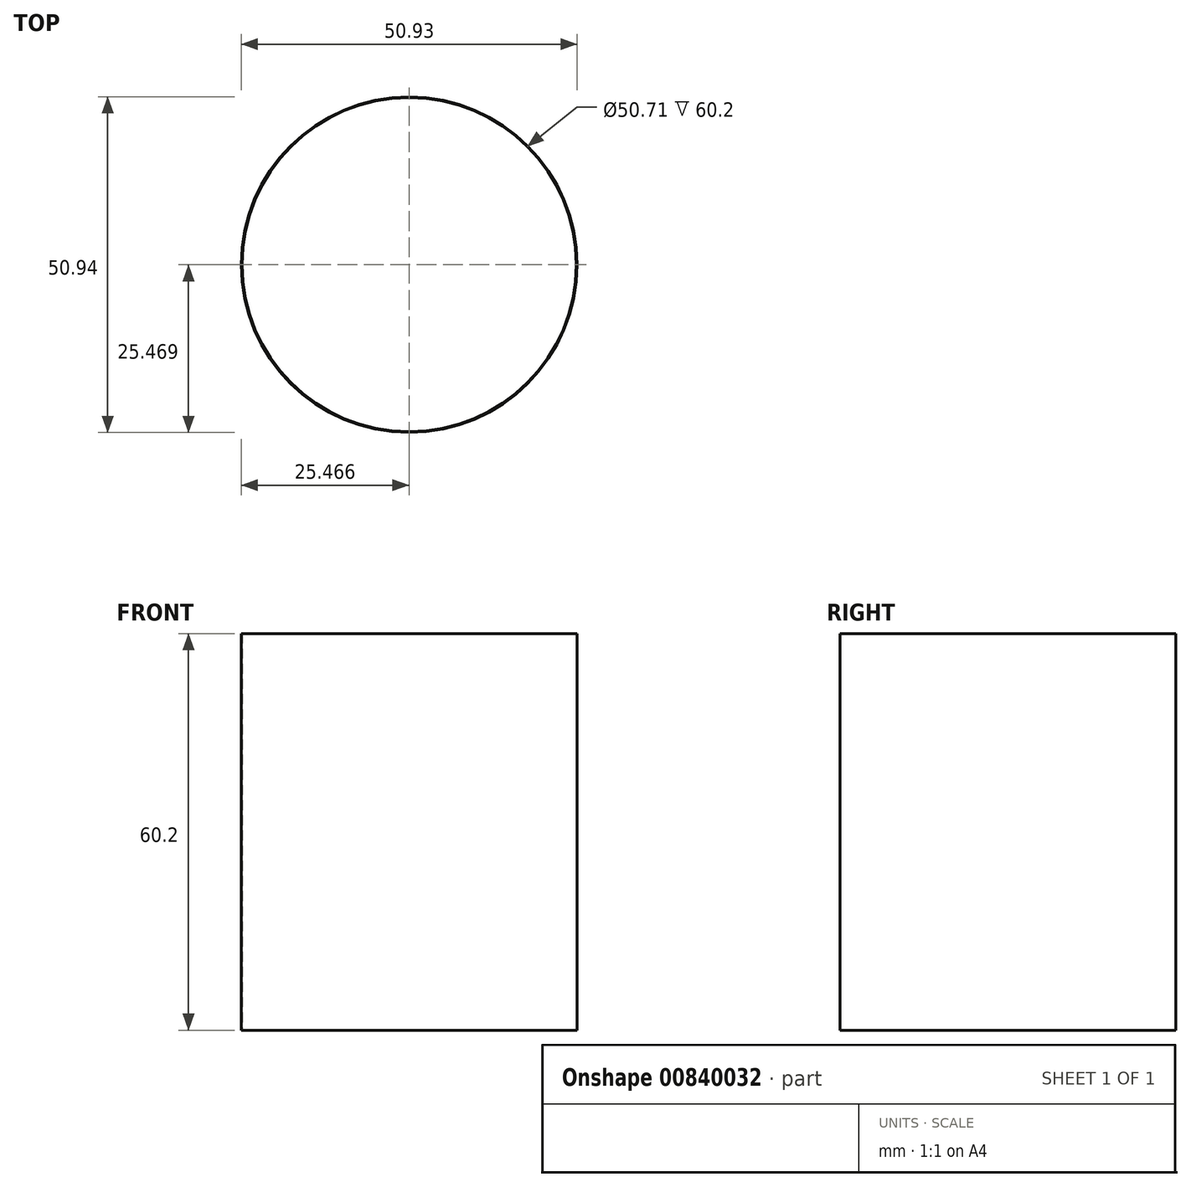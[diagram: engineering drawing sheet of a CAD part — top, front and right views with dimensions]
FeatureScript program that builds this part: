
annotation { "Feature Type Name" : "Feature", "Feature Type Description" : "" }
export const myFeature = defineFeature(function(context is Context, id is Id, definition is map)
    precondition{}
    {
        {
            var Q0;
            Q0=qCreatedBy(makeId("Top.planeOp"),FACE);
            var sketch = newSketch(context, id + "F0", { "sketchPlane" : qUnion([Q0])});
            skCircle(sketch, "E0", {"center": v(-97.55, 10.46) * mm, "radius": 25.47 * mm});
            skCircle(sketch, "E1", {"center": v(-97.55, 10.46) * mm, "radius": 25.35 * mm});
            skSolve(sketch);
        }
        {
            var Q0;
            Q0 = qSketchRegion(id + "F0", true);
            extrude(context, id + "F1", {"entities" : qUnion([Q0]), "depth" : 60.2 * mm, "offsetDistance" : 25 * mm});
        }
    });
